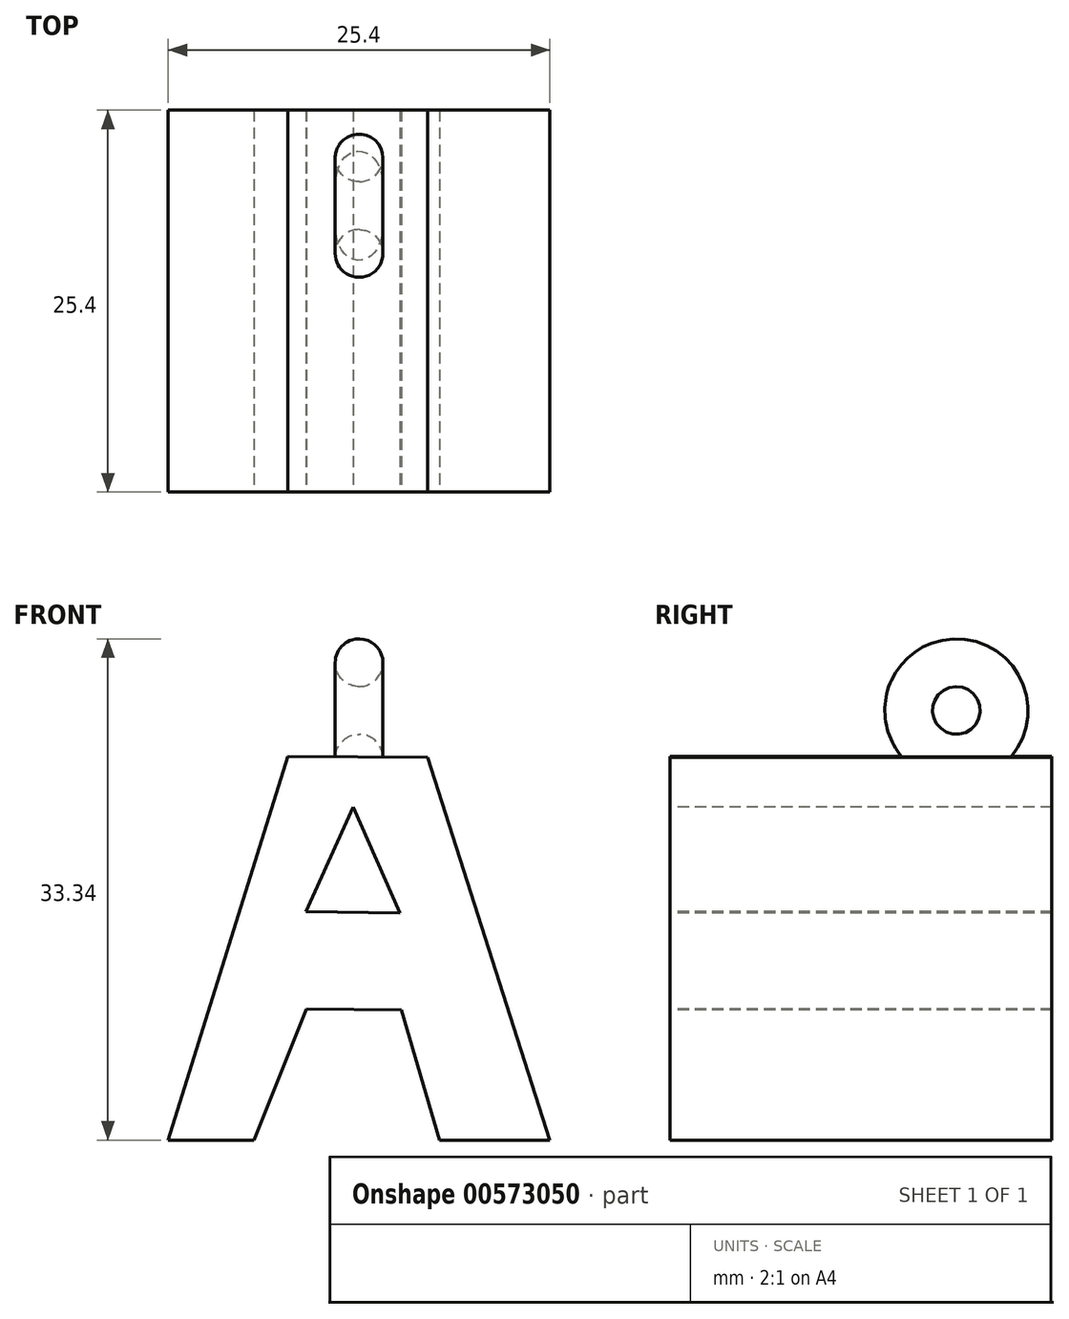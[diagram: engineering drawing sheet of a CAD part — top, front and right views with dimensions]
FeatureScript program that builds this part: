
annotation { "Feature Type Name" : "Feature", "Feature Type Description" : "" }
export const myFeature = defineFeature(function(context is Context, id is Id, definition is map)
    precondition{}
    {
        {
            var Q0;
            Q0=qCreatedBy(makeId("Front.planeOp"),FACE);
            var sketch = newSketch(context, id + "F0", { "sketchPlane" : qUnion([Q0])});
            skLineSegment(sketch, "E0", {"start": v(0, 25.58) * mm, "end": v(0, 0) * mm});
            skLineSegment(sketch, "E1", {"start": v(0, 0) * mm, "end": v(25.4, 0) * mm});
            skLineSegment(sketch, "E2", {"start": v(25.4, 0) * mm, "end": v(25.4, 25.4) * mm});
            skLineSegment(sketch, "E3", {"start": v(25.4, 25.4) * mm, "end": v(0, 25.58) * mm});
            skSolve(sketch);
        }
        {
            var Q0;
            Q0 = qSketchRegion(id + "F0", true);
            extrude(context, id + "F1", {"entities" : qUnion([Q0]), "depth" : 25.4 * mm, "offsetDistance" : 25.4 * mm});
        }
        {
            var Q0;
            Q0=makeQuery(id+"F1.opExtrude","CAP_FACE",FACE,{"disambiguationData":[OSD([sQuery(id+"F0.wireOp",EDGE,"E0"),sQuery(id+"F0.wireOp",EDGE,"E1"),sQuery(id+"F0.wireOp",EDGE,"E2"),sQuery(id+"F0.wireOp",EDGE,"E3")])],"isStart":false});
            var sketch = newSketch(context, id + "F2", { "sketchPlane" : qUnion([Q0])});
            skLineSegment(sketch, "E4", {"start": v(7.96, 25.53) * mm, "end": v(0, 0) * mm});
            skLineSegment(sketch, "E5", {"start": v(17.27, 25.46) * mm, "end": v(25.4, 0) * mm});
            skLineSegment(sketch, "E6", {"start": v(15.41, 15.1) * mm, "end": v(12.3, 22.14) * mm});
            skLineSegment(sketch, "E7", {"start": v(12.3, 22.14) * mm, "end": v(9.18, 15.18) * mm});
            skLineSegment(sketch, "E8", {"start": v(9.18, 15.18) * mm, "end": v(15.41, 15.1) * mm});
            skLineSegment(sketch, "E9", {"start": v(18.07, 0) * mm, "end": v(15.53, 8.66) * mm});
            skLineSegment(sketch, "E10", {"start": v(15.53, 8.66) * mm, "end": v(9.2, 8.72) * mm});
            skLineSegment(sketch, "E11", {"start": v(9.2, 8.72) * mm, "end": v(5.7, 0) * mm});
            skSolve(sketch);
        }
        {
            var Q0;
            {var subQ0=sQuery(id+"F2.wireOp",EDGE,"E4");Q0=makeQuery(id+"F2.imprint","IMPRINT",FACE,{"disambiguationData":[TD([[makeQuery(id+"F2.imprint","IMPRINT",EDGE,{"derivedFrom":subQ0}),-1.0]])]});}
            var Q1;
            {var subQ0=sQuery(id+"F2.wireOp",EDGE,"E9");Q1=makeQuery(id+"F2.imprint","IMPRINT",FACE,{"disambiguationData":[TD([[makeQuery(id+"F2.imprint","IMPRINT",EDGE,{"derivedFrom":subQ0}),1.0]])]});}
            var Q2;
            {var subQ0=sQuery(id+"F2.wireOp",EDGE,"E5");Q2=makeQuery(id+"F2.imprint","IMPRINT",FACE,{"disambiguationData":[TD([[makeQuery(id+"F2.imprint","IMPRINT",EDGE,{"derivedFrom":subQ0}),1.0]])]});}
            var Q3;
            Q3=makeQuery(id+"F2.imprint","IMPRINT",FACE,{"disambiguationData":[TD([[makeQuery(id+"F2.imprint","IMPRINT",EDGE,{"derivedFrom":sQuery(id+"F2.wireOp",EDGE,"E6")}),1.0]])]});
            extrude(context, id + "F3", {"entities" : qUnion([Q0, Q1, Q2, Q3]), "operationType" : NewBodyOperationType.REMOVE, "oppositeDirection" : true, "depth" : 25.4 * mm, "offsetDistance" : 25.4 * mm});
        }
        {
            var Q0;
            Q0=qCreatedBy(makeId("Front.planeOp"),FACE);
            cPlane(context, id + "F4", {"entities" : qUnion([Q0]), "cplaneType" : CPlaneType.OFFSET, "offset" : 6.35 * mm, "width" : 152.4 * mm, "height" : 152.4 * mm});
        }
        {
            var Q0;
            Q0=qCreatedBy(id+"F4.planeOp",FACE);
            var sketch = newSketch(context, id + "F5", { "sketchPlane" : qUnion([Q0])});
            skCircle(sketch, "E12", {"center": v(12.7, 25.4) * mm, "radius": 1.59 * mm});
            skLineSegment(sketch, "E13", {"start": v(0, 28.58) * mm, "end": v(28.5, 28.58) * mm});
            skSolve(sketch);
        }
        {
            var Q0;
            Q0 = qSketchRegion(id + "F5", true);
            var Q1;
            Q1=sQuery(id+"F5.wireOp",EDGE,"E13");
            revolve(context, id + "F6", {"operationType" : NewBodyOperationType.ADD, "entities" : qUnion([Q0]), "axis" : qUnion([Q1]), "revolveType" : RevolveType.FULL});
        }
    });
